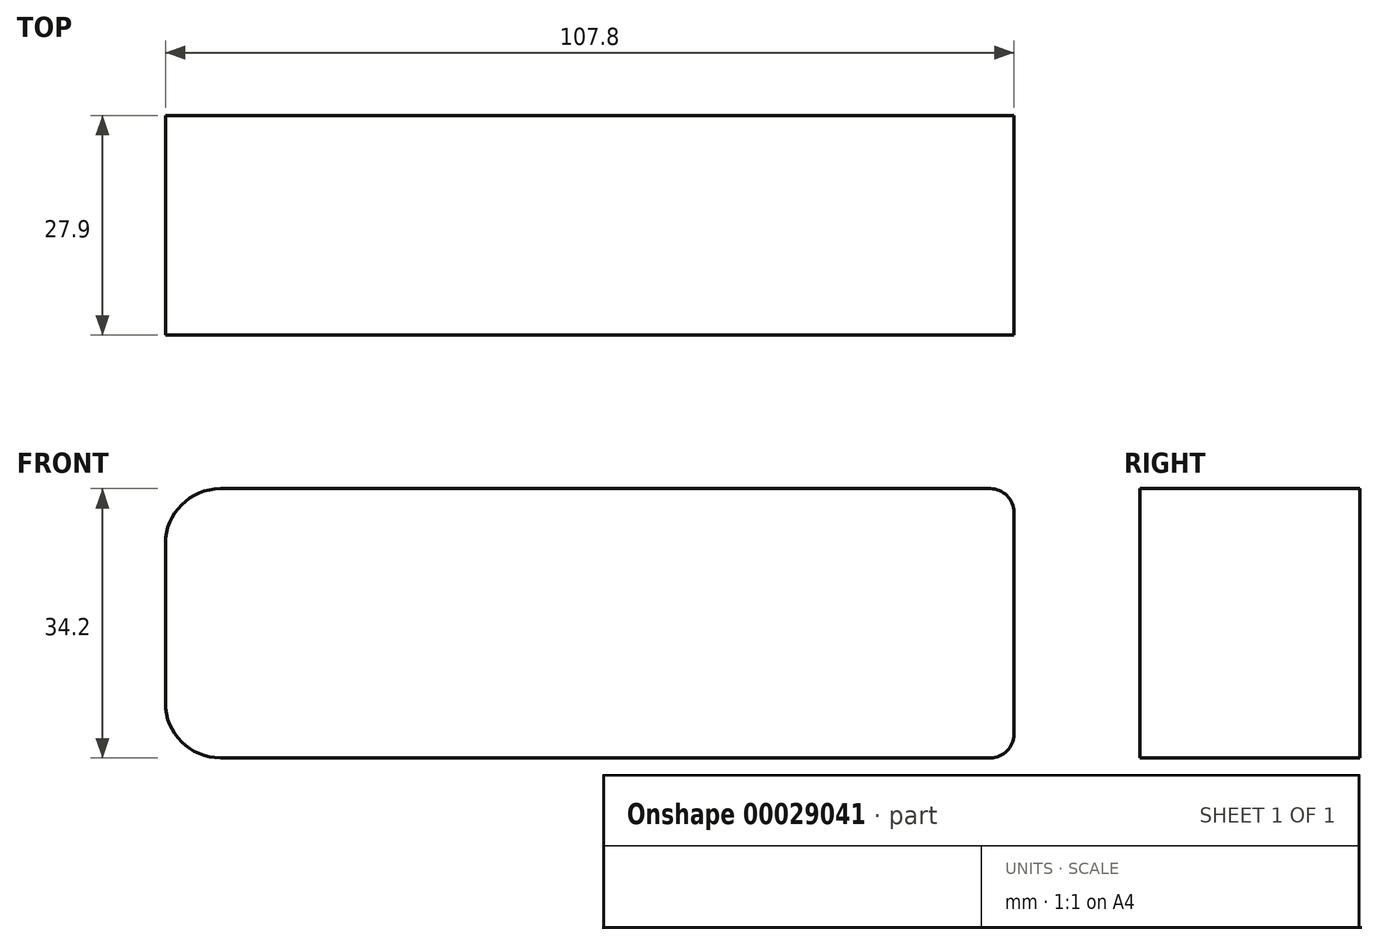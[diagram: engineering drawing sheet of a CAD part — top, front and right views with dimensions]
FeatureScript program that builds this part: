
annotation { "Feature Type Name" : "Feature", "Feature Type Description" : "" }
export const myFeature = defineFeature(function(context is Context, id is Id, definition is map)
    precondition{}
    {
        {
            var Q0;
            Q0=qCreatedBy(makeId("Top.planeOp"),FACE);
            var sketch = newSketch(context, id + "F0", { "sketchPlane" : qUnion([Q0])});
            skLineSegment(sketch, "E0.rect.bottom", {"start": v(53.9, -13.95) * mm, "end": v(-53.9, -13.95) * mm});
            skLineSegment(sketch, "E0.rect.top", {"start": v(53.9, 13.95) * mm, "end": v(-53.9, 13.95) * mm});
            skLineSegment(sketch, "E0.rect.left", {"start": v(53.9, -13.95) * mm, "end": v(53.9, 13.95) * mm});
            skLineSegment(sketch, "E0.rect.right", {"start": v(-53.9, -13.95) * mm, "end": v(-53.9, 13.95) * mm});
            skPoint(sketch, "E0.rect.middle", {"position": v(0, 0) * mm});
            skSolve(sketch);
        }
        {
            var Q0;
            Q0=qSketchRegion(id+"F0",true);
            extrude(context, id + "F1", {"entities" : qUnion([Q0]), "depth" : 34.2 * mm});
        }
        {
            var Q0;
            Q0=makeQuery(id+"F1.opExtrude","CAP_EDGE",EDGE,{"disambiguationData":[OSD([sQuery(id+"F0.wireOp",EDGE,"E0.rect.right")])],"isStart":false});
            var Q1;
            Q1=makeQuery(id+"F1.opExtrude","CAP_EDGE",EDGE,{"disambiguationData":[OSD([sQuery(id+"F0.wireOp",EDGE,"E0.rect.right")])],"isStart":true});
            fillet(context, id + "F2", {"entities" : qUnion([Q0, Q1]), "radius" : 7 * mm, "tangentPropagation" : true, "allowEdgeOverflow" : false});
        }
        {
            var Q0;
            Q0=makeQuery(id+"F1.opExtrude","CAP_EDGE",EDGE,{"disambiguationData":[OSD([sQuery(id+"F0.wireOp",EDGE,"E0.rect.left")])],"isStart":false});
            var Q1;
            Q1=makeQuery(id+"F1.opExtrude","CAP_EDGE",EDGE,{"disambiguationData":[OSD([sQuery(id+"F0.wireOp",EDGE,"E0.rect.left")])],"isStart":true});
            fillet(context, id + "F3", {"entities" : qUnion([Q0, Q1]), "radius" : 3 * mm, "tangentPropagation" : true, "allowEdgeOverflow" : false});
        }
    });
